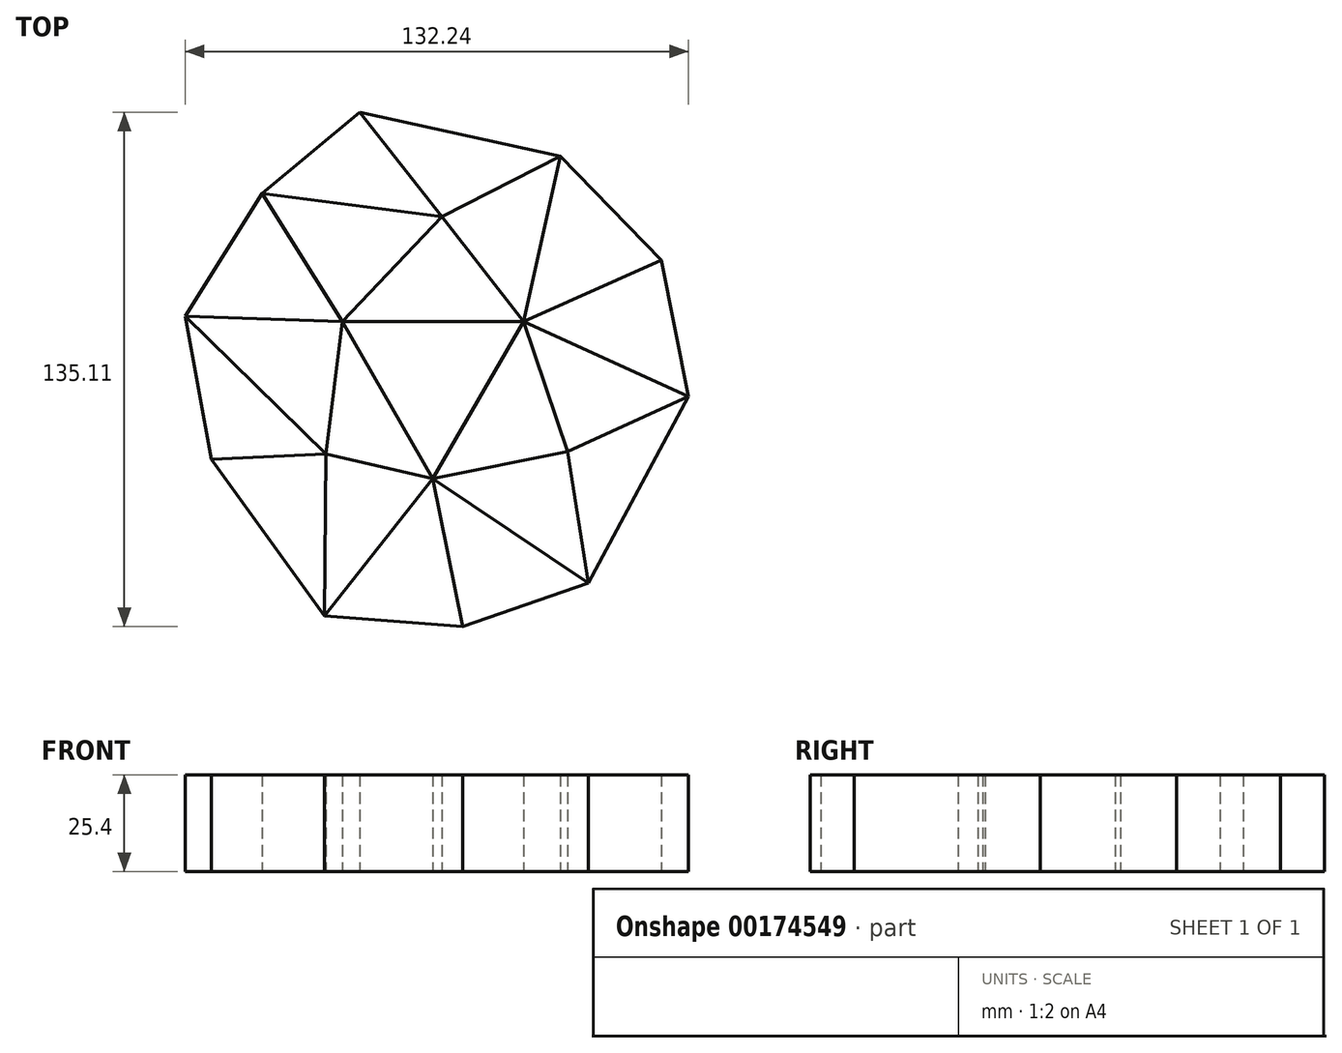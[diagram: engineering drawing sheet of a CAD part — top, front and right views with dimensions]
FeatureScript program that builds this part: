
annotation { "Feature Type Name" : "Feature", "Feature Type Description" : "" }
export const myFeature = defineFeature(function(context is Context, id is Id, definition is map)
    precondition{}
    {
        {
            var Q0;
            Q0=qCreatedBy(makeId("Top.planeOp"),FACE);
            var sketch = newSketch(context, id + "F0", { "sketchPlane" : qUnion([Q0])});
            skCircle(sketch, "E0.cCircle", {"center": v(-74.48, -16.83) * mm, "radius": 13.75 * mm, "construction": true});
            skLineSegment(sketch, "E0.0", {"start": v(-74.48, -44.32) * mm, "end": v(-98.3, -3.08) * mm});
            skLineSegment(sketch, "E0.1", {"start": v(-98.3, -3.08) * mm, "end": v(-50.67, -3.08) * mm});
            skLineSegment(sketch, "E0.2", {"start": v(-50.67, -3.08) * mm, "end": v(-74.48, -44.32) * mm});
            skLineSegment(sketch, "E1", {"start": v(-74.48, -16.83) * mm, "end": v(-74.48, -44.32) * mm, "construction": true});
            skLineSegment(sketch, "E2", {"start": v(-93.72, 51.9) * mm, "end": v(-41, 40.3) * mm});
            skLineSegment(sketch, "E3", {"start": v(-41, 40.3) * mm, "end": v(-14.4, 13.04) * mm});
            skLineSegment(sketch, "E4", {"start": v(-14.4, 13.04) * mm, "end": v(-7.31, -22.79) * mm});
            skLineSegment(sketch, "E5", {"start": v(-7.31, -22.79) * mm, "end": v(-33.62, -71.75) * mm});
            skLineSegment(sketch, "E6", {"start": v(-33.62, -71.75) * mm, "end": v(-66.6, -83.22) * mm});
            skLineSegment(sketch, "E7", {"start": v(-66.6, -83.22) * mm, "end": v(-103.02, -80.45) * mm});
            skLineSegment(sketch, "E8", {"start": v(-103.02, -80.45) * mm, "end": v(-132.72, -39.23) * mm});
            skLineSegment(sketch, "E9", {"start": v(-132.72, -39.23) * mm, "end": v(-139.55, -1.75) * mm});
            skLineSegment(sketch, "E10", {"start": v(-139.55, -1.75) * mm, "end": v(-119.36, 30.56) * mm});
            skLineSegment(sketch, "E11", {"start": v(-119.36, 30.56) * mm, "end": v(-93.72, 51.9) * mm});
            skLineSegment(sketch, "E12", {"start": v(-41, 40.3) * mm, "end": v(-50.67, -3.08) * mm});
            skLineSegment(sketch, "E13", {"start": v(-14.4, 13.04) * mm, "end": v(-50.67, -3.08) * mm});
            skLineSegment(sketch, "E14", {"start": v(-50.67, -3.08) * mm, "end": v(-7.31, -22.79) * mm});
            skLineSegment(sketch, "E15", {"start": v(-119.36, 30.56) * mm, "end": v(-98.3, -3.08) * mm});
            skLineSegment(sketch, "E16", {"start": v(-139.55, -1.75) * mm, "end": v(-98.3, -3.08) * mm});
            skLineSegment(sketch, "E17", {"start": v(-103.02, -80.45) * mm, "end": v(-74.48, -44.32) * mm});
            skLineSegment(sketch, "E18", {"start": v(-66.6, -83.22) * mm, "end": v(-74.48, -44.32) * mm});
            skLineSegment(sketch, "E19", {"start": v(-33.62, -71.75) * mm, "end": v(-74.48, -44.32) * mm});
            skLineSegment(sketch, "E20", {"start": v(-98.3, -3.08) * mm, "end": v(-102.59, -37.9) * mm});
            skLineSegment(sketch, "E21", {"start": v(-102.59, -37.9) * mm, "end": v(-139.55, -1.75) * mm});
            skLineSegment(sketch, "E22", {"start": v(-132.72, -39.23) * mm, "end": v(-102.59, -37.9) * mm});
            skLineSegment(sketch, "E23", {"start": v(-103.02, -80.45) * mm, "end": v(-102.59, -37.9) * mm});
            skLineSegment(sketch, "E24", {"start": v(-102.59, -37.9) * mm, "end": v(-74.48, -44.32) * mm});
            skLineSegment(sketch, "E25", {"start": v(-50.67, -3.08) * mm, "end": v(-39.1, -37.25) * mm});
            skLineSegment(sketch, "E26", {"start": v(-39.1, -37.25) * mm, "end": v(-7.31, -22.79) * mm});
            skLineSegment(sketch, "E27", {"start": v(-33.62, -71.75) * mm, "end": v(-39.1, -37.25) * mm});
            skLineSegment(sketch, "E28", {"start": v(-39.1, -37.25) * mm, "end": v(-74.48, -44.32) * mm});
            skLineSegment(sketch, "E29", {"start": v(-93.72, 51.9) * mm, "end": v(-72.12, 24.45) * mm});
            skLineSegment(sketch, "E30", {"start": v(-72.12, 24.45) * mm, "end": v(-98.3, -3.08) * mm});
            skLineSegment(sketch, "E31", {"start": v(-41, 40.3) * mm, "end": v(-72.12, 24.45) * mm});
            skLineSegment(sketch, "E32", {"start": v(-50.67, -3.08) * mm, "end": v(-72.12, 24.45) * mm});
            skLineSegment(sketch, "E33", {"start": v(-119.36, 30.56) * mm, "end": v(-72.12, 24.45) * mm});
            skSolve(sketch);
        }
        {
            var Q0;
            Q0=makeQuery(id+"F0.imprint","IMPRINT",FACE,{"disambiguationData":[TD([[makeQuery(id+"F0.imprint","IMPRINT",EDGE,{"derivedFrom":sQuery(id+"F0.wireOp",EDGE,"E10")}),-1.0]])]});
            var Q1;
            Q1=makeQuery(id+"F0.imprint","IMPRINT",FACE,{"disambiguationData":[TD([[makeQuery(id+"F0.imprint","IMPRINT",EDGE,{"derivedFrom":sQuery(id+"F0.wireOp",EDGE,"E0.0")}),1.0]])]});
            var Q2;
            Q2=makeQuery(id+"F0.imprint","IMPRINT",FACE,{"disambiguationData":[TD([[makeQuery(id+"F0.imprint","IMPRINT",EDGE,{"derivedFrom":sQuery(id+"F0.wireOp",EDGE,"E8")}),-1.0]])]});
            var Q3;
            Q3=makeQuery(id+"F0.imprint","IMPRINT",FACE,{"disambiguationData":[TD([[makeQuery(id+"F0.imprint","IMPRINT",EDGE,{"derivedFrom":sQuery(id+"F0.wireOp",EDGE,"E7")}),-1.0]])]});
            var Q4;
            Q4=makeQuery(id+"F0.imprint","IMPRINT",FACE,{"disambiguationData":[TD([[makeQuery(id+"F0.imprint","IMPRINT",EDGE,{"derivedFrom":sQuery(id+"F0.wireOp",EDGE,"E19")}),-1.0]])]});
            var Q5;
            Q5=makeQuery(id+"F0.imprint","IMPRINT",FACE,{"disambiguationData":[TD([[makeQuery(id+"F0.imprint","IMPRINT",EDGE,{"derivedFrom":sQuery(id+"F0.wireOp",EDGE,"E14")}),-1.0]])]});
            var Q6;
            Q6=makeQuery(id+"F0.imprint","IMPRINT",FACE,{"disambiguationData":[TD([[makeQuery(id+"F0.imprint","IMPRINT",EDGE,{"derivedFrom":sQuery(id+"F0.wireOp",EDGE,"E3")}),-1.0]])]});
            var Q7;
            Q7=makeQuery(id+"F0.imprint","IMPRINT",FACE,{"disambiguationData":[TD([[makeQuery(id+"F0.imprint","IMPRINT",EDGE,{"derivedFrom":sQuery(id+"F0.wireOp",EDGE,"E2")}),-1.0]])]});
            var Q8;
            Q8=makeQuery(id+"F0.imprint","IMPRINT",FACE,{"disambiguationData":[TD([[makeQuery(id+"F0.imprint","IMPRINT",EDGE,{"derivedFrom":sQuery(id+"F0.wireOp",EDGE,"E0.1")}),1.0]])]});
            extrude(context, id + "F1", {"entities" : qUnion([Q0, Q1, Q2, Q3, Q4, Q5, Q6, Q7, Q8]), "depth" : 25.4 * mm});
        }
        {
            var Q0;
            Q0=makeQuery(id+"F0.imprint","IMPRINT",FACE,{"disambiguationData":[TD([[makeQuery(id+"F0.imprint","IMPRINT",EDGE,{"derivedFrom":sQuery(id+"F0.wireOp",EDGE,"E11")}),-1.0]])]});
            var Q1;
            Q1=makeQuery(id+"F0.imprint","IMPRINT",FACE,{"disambiguationData":[TD([[makeQuery(id+"F0.imprint","IMPRINT",EDGE,{"derivedFrom":sQuery(id+"F0.wireOp",EDGE,"E12")}),-1.0]])]});
            var Q2;
            Q2=makeQuery(id+"F0.imprint","IMPRINT",FACE,{"disambiguationData":[TD([[makeQuery(id+"F0.imprint","IMPRINT",EDGE,{"derivedFrom":sQuery(id+"F0.wireOp",EDGE,"E4")}),-1.0]])]});
            var Q3;
            Q3=makeQuery(id+"F0.imprint","IMPRINT",FACE,{"disambiguationData":[TD([[makeQuery(id+"F0.imprint","IMPRINT",EDGE,{"derivedFrom":sQuery(id+"F0.wireOp",EDGE,"E5")}),-1.0]])]});
            var Q4;
            Q4=makeQuery(id+"F0.imprint","IMPRINT",FACE,{"disambiguationData":[TD([[makeQuery(id+"F0.imprint","IMPRINT",EDGE,{"derivedFrom":sQuery(id+"F0.wireOp",EDGE,"E0.2")}),1.0]])]});
            var Q5;
            Q5=makeQuery(id+"F0.imprint","IMPRINT",FACE,{"disambiguationData":[TD([[makeQuery(id+"F0.imprint","IMPRINT",EDGE,{"derivedFrom":sQuery(id+"F0.wireOp",EDGE,"E6")}),-1.0]])]});
            var Q6;
            Q6=makeQuery(id+"F0.imprint","IMPRINT",FACE,{"disambiguationData":[TD([[makeQuery(id+"F0.imprint","IMPRINT",EDGE,{"derivedFrom":sQuery(id+"F0.wireOp",EDGE,"E17")}),1.0]])]});
            var Q7;
            Q7=makeQuery(id+"F0.imprint","IMPRINT",FACE,{"disambiguationData":[TD([[makeQuery(id+"F0.imprint","IMPRINT",EDGE,{"derivedFrom":sQuery(id+"F0.wireOp",EDGE,"E9")}),-1.0]])]});
            extrude(context, id + "F2", {"entities" : qUnion([Q0, Q1, Q2, Q3, Q4, Q5, Q6, Q7]), "depth" : 25.4 * mm});
        }
        {
            var Q0;
            Q0=makeQuery(id+"F0.imprint","IMPRINT",FACE,{"disambiguationData":[TD([[makeQuery(id+"F0.imprint","IMPRINT",EDGE,{"derivedFrom":sQuery(id+"F0.wireOp",EDGE,"E16")}),-1.0]])]});
            var Q1;
            Q1=makeQuery(id+"F0.imprint","IMPRINT",FACE,{"disambiguationData":[TD([[makeQuery(id+"F0.imprint","IMPRINT",EDGE,{"derivedFrom":sQuery(id+"F0.wireOp",EDGE,"E15")}),1.0]])]});
            extrude(context, id + "F3", {"entities" : qUnion([Q0, Q1]), "depth" : 25.4 * mm});
        }
    });
